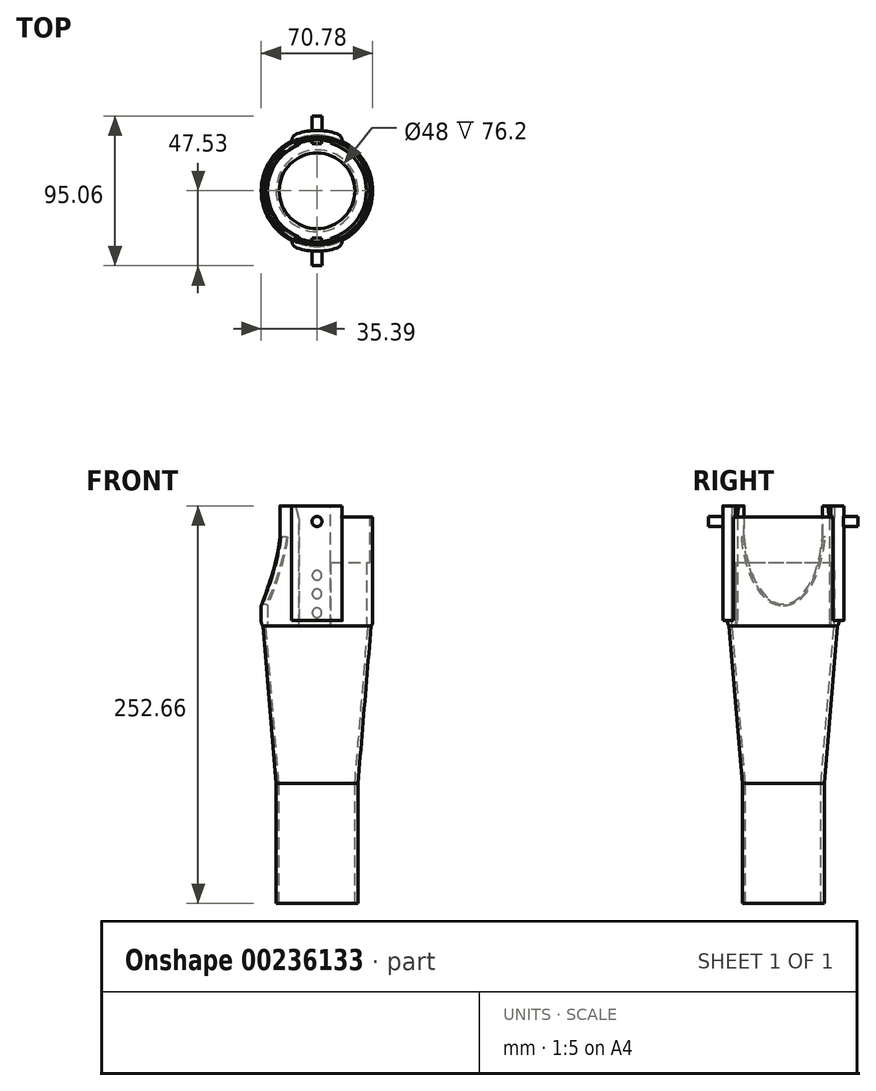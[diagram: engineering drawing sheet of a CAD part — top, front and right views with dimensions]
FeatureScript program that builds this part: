
annotation { "Feature Type Name" : "Feature", "Feature Type Description" : "" }
export const myFeature = defineFeature(function(context is Context, id is Id, definition is map)
    precondition{}
    {
        {
            var Q0;
            Q0=qCreatedBy(makeId("Top.planeOp"),FACE);
            var sketch = newSketch(context, id + "F0", { "sketchPlane" : qUnion([Q0])});
            skCircle(sketch, "E0", {"center": v(0, 0) * mm, "radius": 26 * mm});
            skSolve(sketch);
        }
        {
            var Q0;
            Q0=makeQuery(id+"F0.imprint","IMPRINT",FACE,{"disambiguationData":[TD([[makeQuery(id+"F0.imprint","IMPRINT",EDGE,{"derivedFrom":sQuery(id+"F0.wireOp",EDGE,"E0")}),1.0]])]});
            extrude(context, id + "F1", {"entities" : qUnion([Q0]), "depth" : 76.2 * mm});
        }
        {
            var Q0;
            Q0=makeQuery(id+"F1.opExtrude","CAP_FACE",FACE,{"disambiguationData":[OSD([sQuery(id+"F0.wireOp",EDGE,"E0")])],"isStart":false});
            cPlane(context, id + "F2", {"entities" : qUnion([Q0]), "cplaneType" : CPlaneType.OFFSET, "offset" : 0 * mm, "width" : 150 * mm, "height" : 150 * mm});
        }
        {
            var Q0;
            Q0=qCreatedBy(id+"F2.planeOp",FACE);
            var sketch = newSketch(context, id + "F3", { "sketchPlane" : qUnion([Q0])});
            skCircle(sketch, "E1.0", {"center": v(0, 0) * mm, "radius": 26 * mm});
            skSolve(sketch);
        }
        {
            var Q0;
            Q0=qCreatedBy(id+"F2.planeOp",FACE);
            cPlane(context, id + "F4", {"entities" : qUnion([Q0]), "cplaneType" : CPlaneType.OFFSET, "offset" : 100 * mm, "width" : 150 * mm, "height" : 150 * mm});
        }
        {
            var Q0;
            Q0=qCreatedBy(id+"F4.planeOp",FACE);
            var sketch = newSketch(context, id + "F5", { "sketchPlane" : qUnion([Q0])});
            skCircle(sketch, "E2", {"center": v(0, 0) * mm, "radius": 34.38 * mm});
            skSolve(sketch);
        }
        {
            var Q1;
            Q1=makeQuery(id+"F3.imprint","IMPRINT",FACE,{"disambiguationData":[TD([[makeQuery(id+"F3.imprint","IMPRINT",EDGE,{"derivedFrom":sQuery(id+"F3.wireOp",EDGE,"E1.0")}),1.0]])]});
            var Q2;
            Q2=makeQuery(id+"F5.imprint","IMPRINT",FACE,{"disambiguationData":[TD([[makeQuery(id+"F5.imprint","IMPRINT",EDGE,{"derivedFrom":sQuery(id+"F5.wireOp",EDGE,"E2")}),1.0]])]});
            var Q3;
            Q3=sQuery(id+"F5.wireOp",EDGE,"E2");
            var Q4;
            Q4=sQuery(id+"F3.wireOp",EDGE,"E1.0");
            loft(context, id + "F6", {"operationType" : NewBodyOperationType.ADD, "sheetProfilesArray" : [{ "sheetProfileEntities" : qUnion([Q1]) }, { "sheetProfileEntities" : qUnion([Q2]) }], "wireProfilesArray" : [{ "wireProfileEntities" : qUnion([Q3]) }, { "wireProfileEntities" : qUnion([Q4]) }]});
        }
        {
            var Q0;
            Q0=qCreatedBy(id+"F2.planeOp",FACE);
            var sketch = newSketch(context, id + "F7", { "sketchPlane" : qUnion([Q0])});
            skCircle(sketch, "E3", {"center": v(0, 0) * mm, "radius": 24 * mm});
            skSolve(sketch);
        }
        {
            var Q0;
            Q0=qCreatedBy(id+"F4.planeOp",FACE);
            var sketch = newSketch(context, id + "F8", { "sketchPlane" : qUnion([Q0])});
            skCircle(sketch, "E4", {"center": v(0, 0) * mm, "radius": 32.38 * mm});
            skCircle(sketch, "E5.0", {"center": v(0, 0) * mm, "radius": 34.38 * mm, "construction": true});
            skSolve(sketch);
        }
        {
            var Q1;
            Q1=qSketchRegion(id+"F7",true);
            var Q2;
            Q2=qSketchRegion(id+"F8",true);
            loft(context, id + "F9", {"operationType" : NewBodyOperationType.REMOVE, "sheetProfilesArray" : [{ "sheetProfileEntities" : qUnion([Q1]) }, { "sheetProfileEntities" : qUnion([Q2]) }]});
        }
        {
            var Q0;
            Q0=qCreatedBy(makeId("Top.planeOp"),FACE);
            var sketch = newSketch(context, id + "F10", { "sketchPlane" : qUnion([Q0])});
            skCircle(sketch, "E6", {"center": v(0, 0) * mm, "radius": 24 * mm});
            skSolve(sketch);
        }
        {
            var Q1;
            Q1=qSketchRegion(id+"F7",true);
            var Q2;
            Q2=qSketchRegion(id+"F10",true);
            loft(context, id + "F11", {"operationType" : NewBodyOperationType.REMOVE, "sheetProfilesArray" : [{ "sheetProfileEntities" : qUnion([Q1]) }, { "sheetProfileEntities" : qUnion([Q2]) }]});
        }
        {
            var Q0;
            Q0=qCreatedBy(id+"F4.planeOp",FACE);
            var sketch = newSketch(context, id + "F12", { "sketchPlane" : qUnion([Q0])});
            skCircle(sketch, "E7.0", {"center": v(0, 0) * mm, "radius": 32.38 * mm, "construction": true});
            skCircle(sketch, "E8.0", {"center": v(0, 0) * mm, "radius": 34.38 * mm, "construction": true});
            skCircle(sketch, "E9", {"center": v(0, 0) * mm, "radius": 31.38 * mm});
            skCircle(sketch, "E10", {"center": v(0, 0) * mm, "radius": 35.38 * mm});
            skSolve(sketch);
        }
        {
            var Q0;
            Q0=qSketchRegion(id+"F12",true);
            extrude(context, id + "F13", {"entities" : qUnion([Q0]), "operationType" : NewBodyOperationType.ADD, "depth" : 56.46 * mm});
        }
        {
            var Q0;
            Q0=makeQuery(id+"F13.opExtrude","CAP_EDGE",EDGE,{"disambiguationData":[OSD([sQuery(id+"F12.wireOp",EDGE,"E10")])],"isStart":true});
            fillet(context, id + "F14", {"entities" : qUnion([Q0]), "radius" : 5 * mm, "tangentPropagation" : true, "allowEdgeOverflow" : false});
        }
        {
            var Q0;
            Q0=makeQuery(id+"F13.opExtrude","CAP_FACE",FACE,{"disambiguationData":[OSD([sQuery(id+"F12.wireOp",EDGE,"E9"),sQuery(id+"F12.wireOp",EDGE,"E10")])],"isStart":false});
            cPlane(context, id + "F15", {"entities" : qUnion([Q0]), "cplaneType" : CPlaneType.OFFSET, "offset" : 0 * mm, "width" : 150 * mm, "height" : 150 * mm});
        }
        {
            var Q0;
            Q0=qCreatedBy(id+"F15.planeOp",FACE);
            var sketch = newSketch(context, id + "F16", { "sketchPlane" : qUnion([Q0])});
            skArc(sketch, "E11", {"start": v(8.5, -32.53) * mm, "mid": v(33.63, 0) * mm, "end": v(8.5, 32.53) * mm});
            skArc(sketch, "E12", {"start": v(8.5, -27.2) * mm, "mid": v(28.5, 0) * mm, "end": v(8.5, 27.2) * mm});
            skLineSegment(sketch, "E13", {"start": v(0, 46.86) * mm, "end": v(0, -51.58) * mm, "construction": true});
            skLineSegment(sketch, "E14", {"start": v(8.5, 46.54) * mm, "end": v(8.5, -40.4) * mm, "construction": true});
            skLineSegment(sketch, "E15", {"start": v(8.5, 27.2) * mm, "end": v(8.5, 32.53) * mm});
            skLineSegment(sketch, "E16", {"start": v(8.5, -32.53) * mm, "end": v(8.5, -27.2) * mm});
            skSolve(sketch);
        }
        {
            var Q0;
            Q0=qSketchRegion(id+"F16",true);
            extrude(context, id + "F17", {"entities" : qUnion([Q0]), "operationType" : NewBodyOperationType.REMOVE, "oppositeDirection" : true, "depth" : 16 * mm});
        }
        {
            var Q0;
            Q0=qCreatedBy(id+"F15.planeOp",FACE);
            var sketch = newSketch(context, id + "F18", { "sketchPlane" : qUnion([Q0])});
            skPoint(sketch, "E17.0", {"position": v(8.5, 32.53) * mm});
            skPoint(sketch, "E18.0", {"position": v(8.5, -32.53) * mm});
            skLineSegment(sketch, "E19.bottom", {"start": v(8.5, 32.53) * mm, "end": v(-11.5, 32.53) * mm});
            skLineSegment(sketch, "E19.top", {"start": v(8.5, 22.91) * mm, "end": v(-11.5, 22.91) * mm});
            skLineSegment(sketch, "E19.left", {"start": v(8.5, 32.53) * mm, "end": v(8.5, 22.91) * mm});
            skLineSegment(sketch, "E19.right", {"start": v(-11.5, 32.53) * mm, "end": v(-11.5, 22.91) * mm});
            skLineSegment(sketch, "E20.bottom", {"start": v(8.5, -32.53) * mm, "end": v(-11.5, -32.53) * mm});
            skLineSegment(sketch, "E20.top", {"start": v(8.5, -22) * mm, "end": v(-11.5, -22) * mm});
            skLineSegment(sketch, "E20.left", {"start": v(8.5, -32.53) * mm, "end": v(8.5, -22) * mm});
            skLineSegment(sketch, "E20.right", {"start": v(-11.5, -32.53) * mm, "end": v(-11.5, -22) * mm});
            skSolve(sketch);
        }
        {
            var Q0;
            Q0=qSketchRegion(id+"F18",true);
            extrude(context, id + "F19", {"entities" : qUnion([Q0]), "operationType" : NewBodyOperationType.REMOVE, "oppositeDirection" : true, "depth" : 56.46 * mm});
        }
        {
            var Q0;
            {var subQ0=sQuery(id+"F12.wireOp",EDGE,"E9");Q0=makeQuery(id+"F19.boolean.opBoolean","SPLIT",EDGE,{"disambiguationData":[TD([makeQuery(id+"F19.opExtrude","SWEPT_FACE",FACE,{"disambiguationData":[OSD([sQuery(id+"F18.wireOp",EDGE,"E19.right")])]})])],"derivedFrom":makeQuery(id+"F13.opExtrude","CAP_EDGE",EDGE,{"disambiguationData":[OSD([subQ0])],"isStart":true})});}
            var Q1;
            {var subQ0=sQuery(id+"F12.wireOp",EDGE,"E9");Q1=makeQuery(id+"F19.boolean.opBoolean","SPLIT",EDGE,{"disambiguationData":[TD([makeQuery(id+"F19.opExtrude","SWEPT_FACE",FACE,{"disambiguationData":[OSD([sQuery(id+"F18.wireOp",EDGE,"E19.left")])]})])],"derivedFrom":makeQuery(id+"F13.opExtrude","CAP_EDGE",EDGE,{"disambiguationData":[OSD([subQ0])],"isStart":true})});}
            fillet(context, id + "F20", {"entities" : qUnion([Q0, Q1]), "radius" : 5 * mm, "tangentPropagation" : true, "allowEdgeOverflow" : false});
        }
        {
            var Q0;
            Q0=makeQuery(id+"F19.boolean.opBoolean","COPY",FACE,{"derivedFrom":makeQuery(id+"F19.opExtrude","SWEPT_FACE",FACE,{"disambiguationData":[OSD([sQuery(id+"F18.wireOp",EDGE,"E19.bottom")])]})});
            cPlane(context, id + "F21", {"entities" : qUnion([Q0]), "cplaneType" : CPlaneType.OFFSET, "offset" : 0 * mm, "width" : 150 * mm, "height" : 150 * mm});
        }
        {
            var Q0;
            Q0=qCreatedBy(id+"F21.planeOp",FACE);
            var sketch = newSketch(context, id + "F22", { "sketchPlane" : qUnion([Q0])});
            skLineSegment(sketch, "E21.0.0", {"start": v(8.5, 232.66) * mm, "end": v(-11.5, 232.66) * mm, "construction": true});
            skLineSegment(sketch, "E21.0.1", {"start": v(-11.5, 232.66) * mm, "end": v(-11.5, 176.2) * mm, "construction": true});
            skLineSegment(sketch, "E21.0.2", {"start": v(-11.5, 176.2) * mm, "end": v(8.5, 176.2) * mm, "construction": true});
            skLineSegment(sketch, "E21.0.3", {"start": v(8.5, 176.2) * mm, "end": v(8.5, 216.66) * mm, "construction": true});
            skLineSegment(sketch, "E21.0.4", {"start": v(8.5, 216.66) * mm, "end": v(8.5, 232.66) * mm, "construction": true});
            skLineSegment(sketch, "E22", {"start": v(0, 232.66) * mm, "end": v(0, 176.2) * mm, "construction": true});
            skCircle(sketch, "E23", {"center": v(0, 184.7) * mm, "radius": 3 * mm});
            skCircle(sketch, "E24", {"center": v(0, 196.7) * mm, "radius": 3 * mm});
            skCircle(sketch, "E25", {"center": v(0, 208.45) * mm, "radius": 3 * mm});
            skSolve(sketch);
        }
        {
            var Q0;
            Q0=qSketchRegion(id+"F22",true);
            extrude(context, id + "F23", {"entities" : qUnion([Q0]), "depth" : 2.5 * mm});
        }
        {
            var Q0;
            Q0=makeQuery(id+"F23.opExtrude","SWEPT_BODY",BODY,{"disambiguationData":[OSD([sQuery(id+"F22.wireOp",EDGE,"E25")])]});
            var Q1;
            Q1=makeQuery(id+"F23.opExtrude","SWEPT_BODY",BODY,{"disambiguationData":[OSD([sQuery(id+"F22.wireOp",EDGE,"E24")])]});
            var Q2;
            Q2=makeQuery(id+"F23.opExtrude","SWEPT_BODY",BODY,{"disambiguationData":[OSD([sQuery(id+"F22.wireOp",EDGE,"E23")])]});
            var Q3;
            Q3=qCreatedBy(makeId("Front.planeOp"),FACE);
            mirror(context, id + "F24", {"operationType" : NewBodyOperationType.ADD, "entities" : qUnion([Q0, Q1, Q2]), "mirrorPlane" : qUnion([Q3])});
        }
        {
            var Q0;
            Q0=qCreatedBy(id+"F15.planeOp",FACE);
            var sketch = newSketch(context, id + "F25", { "sketchPlane" : qUnion([Q0])});
            skArc(sketch, "E26.0", {"start": v(16, 31.56) * mm, "mid": v(0, 35.38) * mm, "end": v(-16, 31.56) * mm});
            skArc(sketch, "E27.0", {"start": v(16, 34.9) * mm, "mid": v(0, 38.39) * mm, "end": v(-16, 34.9) * mm});
            skLineSegment(sketch, "E28", {"start": v(0, 53.23) * mm, "end": v(0, -112.73) * mm, "construction": true});
            skLineSegment(sketch, "E29", {"start": v(16, 34.9) * mm, "end": v(16, 31.56) * mm});
            skLineSegment(sketch, "E30.MirrorCS", {"start": v(-16, 34.9) * mm, "end": v(-16, 31.56) * mm});
            skLineSegment(sketch, "E31.trimOffspring", {"start": v(-16, -31.56) * mm, "end": v(-16, -34.9) * mm});
            skLineSegment(sketch, "E32.trimOffspring", {"start": v(16, -31.56) * mm, "end": v(16, -34.9) * mm});
            skArc(sketch, "E33.trimOffspring", {"start": v(-16, -34.9) * mm, "mid": v(0, -38.39) * mm, "end": v(16, -34.9) * mm});
            skArc(sketch, "E34.trimOffspring", {"start": v(-16, -31.56) * mm, "mid": v(0, -35.38) * mm, "end": v(16, -31.56) * mm});
            skSolve(sketch);
        }
        {
            var Q0;
            Q0=makeQuery(id+"F25.imprint","IMPRINT",FACE,{"disambiguationData":[TD([[makeQuery(id+"F25.imprint","IMPRINT",EDGE,{"derivedFrom":sQuery(id+"F25.wireOp",EDGE,"E26.0")}),-1.0]])]});
            var Q1;
            Q1=makeQuery(id+"F25.imprint","IMPRINT",FACE,{"disambiguationData":[TD([[makeQuery(id+"F25.imprint","IMPRINT",EDGE,{"derivedFrom":sQuery(id+"F25.wireOp",EDGE,"E31.trimOffspring")}),1.0]])]});
            extrude(context, id + "F26", {"entities" : qUnion([Q0, Q1]), "operationType" : NewBodyOperationType.ADD, "depth" : 20 * mm, "hasSecondDirection" : true, "secondDirectionOppositeDirection" : true, "secondDirectionDepth" : 53 * mm});
        }
        {
            var Q0;
            Q0=makeQuery(id+"F13.opExtrude","CAP_FACE",FACE,{"disambiguationData":[OSD([sQuery(id+"F12.wireOp",EDGE,"E9"),sQuery(id+"F12.wireOp",EDGE,"E10")])],"isStart":false});
            var sketch = newSketch(context, id + "F27", { "sketchPlane" : qUnion([Q0])});
            skArc(sketch, "E35.0", {"start": v(-11.5, 29.2) * mm, "mid": v(-13.8, 28.2) * mm, "end": v(-16, 27) * mm});
            skArc(sketch, "E36.0", {"start": v(16, 31.56) * mm, "mid": v(0, 35.39) * mm, "end": v(-16, 31.56) * mm});
            skLineSegment(sketch, "E36.1", {"start": v(8.5, 32.53) * mm, "end": v(-11.5, 32.53) * mm});
            skArc(sketch, "E36.2", {"start": v(8.5, -32.53) * mm, "mid": v(12.34, -31.28) * mm, "end": v(16, -29.57) * mm});
            skLineSegment(sketch, "E36.3", {"start": v(-11.5, 32.53) * mm, "end": v(-11.5, 29.2) * mm});
            skArc(sketch, "E37.0", {"start": v(-16, -31.56) * mm, "mid": v(0, -35.38) * mm, "end": v(16, -31.56) * mm});
            skLineSegment(sketch, "E38.0", {"start": v(8.5, -32.53) * mm, "end": v(-11.5, -32.53) * mm});
            skLineSegment(sketch, "E39.0", {"start": v(-11.5, -32.53) * mm, "end": v(-11.5, -29.2) * mm});
            skLineSegment(sketch, "E40", {"start": v(-16, -31.56) * mm, "end": v(-16, -27) * mm});
            skLineSegment(sketch, "E41", {"start": v(16, -31.56) * mm, "end": v(16, -29.57) * mm});
            skLineSegment(sketch, "E42", {"start": v(-16, 31.56) * mm, "end": v(-16, 27) * mm});
            skLineSegment(sketch, "E43", {"start": v(16, 31.56) * mm, "end": v(16, 29.57) * mm});
            skArc(sketch, "E44.trimOffspring", {"start": v(-16, -27) * mm, "mid": v(-13.8, -28.2) * mm, "end": v(-11.5, -29.2) * mm});
            skArc(sketch, "E45.trimOffspring", {"start": v(16, 29.57) * mm, "mid": v(12.34, 31.28) * mm, "end": v(8.5, 32.53) * mm});
            skSolve(sketch);
        }
        {
            var Q0;
            Q0=makeQuery(id+"F27.imprint","IMPRINT",FACE,{"disambiguationData":[TD([[makeQuery(id+"F27.imprint","IMPRINT",EDGE,{"derivedFrom":sQuery(id+"F27.wireOp",EDGE,"E36.2")}),-1.0]])]});
            var Q1;
            Q1=makeQuery(id+"F27.imprint","IMPRINT",FACE,{"disambiguationData":[TD([[makeQuery(id+"F27.imprint","IMPRINT",EDGE,{"derivedFrom":sQuery(id+"F27.wireOp",EDGE,"E35.0")}),-1.0]])]});
            extrude(context, id + "F28", {"entities" : qUnion([Q0, Q1]), "operationType" : NewBodyOperationType.ADD, "depth" : 20 * mm, "hasSecondDirection" : true, "secondDirectionOppositeDirection" : true, "secondDirectionDepth" : 25 * mm});
        }
        {
            var Q0;
            Q0=makeQuery(id+"F26.opExtrude","SWEPT_EDGE",EDGE,{"disambiguationData":[OSD([sQuery(id+"F25.wireOp",EDGE,"E32.trimOffspring"),sQuery(id+"F25.wireOp",EDGE,"E33.trimOffspring")])]});
            var Q1;
            Q1=makeQuery(id+"F26.opExtrude","SWEPT_EDGE",EDGE,{"disambiguationData":[OSD([sQuery(id+"F25.wireOp",EDGE,"E31.trimOffspring"),sQuery(id+"F25.wireOp",EDGE,"E33.trimOffspring")])]});
            var Q2;
            Q2=makeQuery(id+"F26.opExtrude","SWEPT_EDGE",EDGE,{"disambiguationData":[OSD([sQuery(id+"F25.wireOp",EDGE,"E27.0"),sQuery(id+"F25.wireOp",EDGE,"E29")])]});
            var Q3;
            Q3=makeQuery(id+"F26.opExtrude","SWEPT_EDGE",EDGE,{"disambiguationData":[OSD([sQuery(id+"F25.wireOp",EDGE,"E27.0"),sQuery(id+"F25.wireOp",EDGE,"E30.MirrorCS")])]});
            fillet(context, id + "F29", {"entities" : qUnion([Q0, Q1, Q2, Q3]), "radius" : 5 * mm, "tangentPropagation" : true, "allowEdgeOverflow" : false});
        }
        {
            var Q0;
            Q0=makeQuery(id+"F28.opExtrude","SWEPT_EDGE",EDGE,{"disambiguationData":[OSD([sQuery(id+"F12.wireOp",EDGE,"E9"),sQuery(id+"F27.wireOp",EDGE,"E40"),sQuery(id+"F27.wireOp",EDGE,"E44.trimOffspring")])]});
            fillet(context, id + "F30", {"entities" : qUnion([Q0]), "radius" : 1 * mm, "tangentPropagation" : true, "allowEdgeOverflow" : false});
        }
        {
            var Q0;
            Q0=makeQuery(id+"F28.opExtrude","SWEPT_EDGE",EDGE,{"disambiguationData":[OSD([sQuery(id+"F16.wireOp",EDGE,"E11"),sQuery(id+"F27.wireOp",EDGE,"E36.2"),sQuery(id+"F27.wireOp",EDGE,"E41")])]});
            fillet(context, id + "F31", {"entities" : qUnion([Q0]), "radius" : 1 * mm, "tangentPropagation" : true, "allowEdgeOverflow" : false});
        }
        {
            var Q0;
            Q0=makeQuery(id+"F28.opExtrude","SWEPT_EDGE",EDGE,{"disambiguationData":[OSD([sQuery(id+"F16.wireOp",EDGE,"492040e4-c0d6-4e85-9304-9fc9be24122b"),sQuery(id+"F27.wireOp",EDGE,"7227a9f5-6aaa-42c1-b2d3-e79f72207cf60.MirrorCS")])]});
            var Q1;
            Q1=makeQuery(id+"F28.opExtrude","SWEPT_EDGE",EDGE,{"disambiguationData":[OSD([sQuery(id+"F12.wireOp",EDGE,"E9"),sQuery(id+"F27.wireOp",EDGE,"E35.0"),sQuery(id+"F27.wireOp",EDGE,"E42")])]});
            fillet(context, id + "F32", {"entities" : qUnion([Q0, Q1]), "radius" : 1 * mm, "tangentPropagation" : true, "allowEdgeOverflow" : false});
        }
        {
            var Q0;
            Q0=makeQuery(id+"F28.opExtrude","SWEPT_EDGE",EDGE,{"disambiguationData":[OSD([sQuery(id+"F16.wireOp",EDGE,"E11"),sQuery(id+"F27.wireOp",EDGE,"E43"),sQuery(id+"F27.wireOp",EDGE,"E45.trimOffspring")])]});
            fillet(context, id + "F33", {"entities" : qUnion([Q0]), "radius" : 1 * mm, "tangentPropagation" : true, "allowEdgeOverflow" : false});
        }
        {
            var Q0;
            Q0=makeQuery(id+"F28.boolean.opBoolean","MERGE",FACE,{"derivedFrom":[makeQuery(id+"F19.boolean.opBoolean","COPY",FACE,{"derivedFrom":makeQuery(id+"F19.opExtrude","SWEPT_FACE",FACE,{"disambiguationData":[OSD([sQuery(id+"F18.wireOp",EDGE,"E19.bottom")])]})}),makeQuery(id+"F28.opExtrude","SWEPT_FACE",FACE,{"disambiguationData":[OSD([sQuery(id+"F27.wireOp",EDGE,"E36.1")])]})]});
            var sketch = newSketch(context, id + "F34", { "sketchPlane" : qUnion([Q0])});
            skLineSegment(sketch, "E46", {"start": v(0, 258) * mm, "end": v(0, 211.42) * mm, "construction": true});
            skCircle(sketch, "E47", {"center": v(0, 242.66) * mm, "radius": 3.18 * mm});
            skSolve(sketch);
        }
        {
            var Q0;
            Q0=makeQuery(id+"F34.imprint","IMPRINT",FACE,{"disambiguationData":[TD([[makeQuery(id+"F34.imprint","IMPRINT",EDGE,{"derivedFrom":sQuery(id+"F34.wireOp",EDGE,"E47")}),1.0]])]});
            extrude(context, id + "F35", {"entities" : qUnion([Q0]), "oppositeDirection" : true, "depth" : 15 * mm});
        }
        {
            var Q0;
            Q0=makeQuery(id+"F35.opExtrude","SWEPT_BODY",BODY,{"disambiguationData":[OSD([sQuery(id+"F34.wireOp",EDGE,"E47")])]});
            var Q1;
            Q1=qCreatedBy(makeId("Front.planeOp"),FACE);
            mirror(context, id + "F36", {"operationType" : NewBodyOperationType.ADD, "entities" : qUnion([Q0]), "mirrorPlane" : qUnion([Q1])});
        }
        {
            var Q0;
            Q0=qCreatedBy(makeId("Right.planeOp"),FACE);
            cPlane(context, id + "F37", {"entities" : qUnion([Q0]), "cplaneType" : CPlaneType.OFFSET, "offset" : 55 * mm, "oppositeDirection" : true, "width" : 150 * mm, "height" : 150 * mm});
        }
        {
            var Q0;
            Q0=qCreatedBy(id+"F37.planeOp",FACE);
            var sketch = newSketch(context, id + "F38", { "sketchPlane" : qUnion([Q0])});
            skEllipse(sketch, "E48", {"center": v(0, 241.57) * mm, "majorRadius": 25.3 * mm, "minorRadius": 51.5 * mm, "majorAxis": v(-1, 0)});
            skSolve(sketch);
        }
        {
            var Q0;
            Q0=qSketchRegion(id+"F38",true);
            extrude(context, id + "F39", {"entities" : qUnion([Q0]), "operationType" : NewBodyOperationType.REMOVE, "depth" : 40 * mm});
        }
        {
            var Q0;
            Q0=makeQuery(id+"F39.boolean.opBoolean","INTERSECT",EDGE,{"derivedFrom":[makeQuery(id+"F13.opExtrude","SWEPT_FACE",FACE,{"disambiguationData":[OSD([sQuery(id+"F12.wireOp",EDGE,"E10")])]}),makeQuery(id+"F39.opExtrude","SWEPT_FACE",FACE,{"disambiguationData":[OSD([sQuery(id+"F38.wireOp",EDGE,"E48")])]})]});
            var Q1;
            {var subQ1=sQuery(id+"F12.wireOp",EDGE,"E9");Q1=makeQuery(id+"F39.boolean.opBoolean","INTERSECT",EDGE,{"derivedFrom":[makeQuery(id+"F28.boolean.opBoolean","MERGE",FACE,{"derivedFrom":[makeQuery(id+"F19.boolean.opBoolean","SPLIT",FACE,{"disambiguationData":[TD([makeQuery(id+"F19.opExtrude","SWEPT_FACE",FACE,{"disambiguationData":[OSD([sQuery(id+"F18.wireOp",EDGE,"E19.right")])]})])],"derivedFrom":makeQuery(id+"F13.opExtrude","SWEPT_FACE",FACE,{"disambiguationData":[OSD([subQ1])]})}),makeQuery(id+"F28.opExtrude","SWEPT_FACE",FACE,{"disambiguationData":[OSD([sQuery(id+"F27.wireOp",EDGE,"E35.0")])]}),makeQuery(id+"F28.opExtrude","SWEPT_FACE",FACE,{"disambiguationData":[OSD([sQuery(id+"F27.wireOp",EDGE,"E44.trimOffspring")])]})]}),makeQuery(id+"F39.opExtrude","SWEPT_FACE",FACE,{"disambiguationData":[OSD([sQuery(id+"F38.wireOp",EDGE,"E48")])]})]});}
            fillet(context, id + "F40", {"entities" : qUnion([Q0, Q1]), "radius" : 1 * mm, "tangentPropagation" : true, "allowEdgeOverflow" : false});
        }
        {
            var Q0;
            {var subQ1=sQuery(id+"F25.wireOp",EDGE,"E31.trimOffspring");var subQ2=makeQuery(id+"F26.opExtrude","SWEPT_FACE",FACE,{"disambiguationData":[OSD([subQ1])]});var subQ3=sQuery(id+"F12.wireOp",EDGE,"E10");var subQ7=sQuery(id+"F12.wireOp",EDGE,"E9");var subQ8=makeQuery(id+"F13.opExtrude","SWEPT_FACE",FACE,{"disambiguationData":[OSD([subQ7])]});Q0=makeQuery(id+"F39.boolean.opBoolean","SPLIT",FACE,{"disambiguationData":[TD([subQ2])],"derivedFrom":makeQuery(id+"F28.boolean.opBoolean","SPLIT",FACE,{"disambiguationData":[TD([subQ8])],"derivedFrom":makeQuery(id+"F13.opExtrude","CAP_FACE",FACE,{"disambiguationData":[OSD([subQ7,subQ3])],"isStart":false})})});}
            var Q1;
            {var subQ2=sQuery(id+"F25.wireOp",EDGE,"E30.MirrorCS");var subQ3=makeQuery(id+"F26.opExtrude","SWEPT_FACE",FACE,{"disambiguationData":[OSD([subQ2])]});var subQ4=sQuery(id+"F12.wireOp",EDGE,"E10");var subQ7=sQuery(id+"F12.wireOp",EDGE,"E9");var subQ8=makeQuery(id+"F13.opExtrude","SWEPT_FACE",FACE,{"disambiguationData":[OSD([subQ7])]});Q1=makeQuery(id+"F39.boolean.opBoolean","SPLIT",FACE,{"disambiguationData":[TD([subQ3])],"derivedFrom":makeQuery(id+"F28.boolean.opBoolean","SPLIT",FACE,{"disambiguationData":[TD([subQ8])],"derivedFrom":makeQuery(id+"F13.opExtrude","CAP_FACE",FACE,{"disambiguationData":[OSD([subQ7,subQ4])],"isStart":false})})});}
            var Q2;
            Q2=makeQuery(id+"F28.boolean.opBoolean","MERGE",FACE,{"derivedFrom":[makeQuery(id+"F26.opExtrude","CAP_FACE",FACE,{"disambiguationData":[OSD([sQuery(id+"F25.wireOp",EDGE,"E31.trimOffspring"),sQuery(id+"F25.wireOp",EDGE,"E32.trimOffspring"),sQuery(id+"F25.wireOp",EDGE,"E33.trimOffspring"),sQuery(id+"F25.wireOp",EDGE,"E34.trimOffspring")])],"isStart":false}),makeQuery(id+"F28.opExtrude","CAP_FACE",FACE,{"disambiguationData":[OSD([sQuery(id+"F27.wireOp",EDGE,"E36.2"),sQuery(id+"F27.wireOp",EDGE,"E37.0"),sQuery(id+"F27.wireOp",EDGE,"E38.0"),sQuery(id+"F27.wireOp",EDGE,"E39.0"),sQuery(id+"F27.wireOp",EDGE,"E40"),sQuery(id+"F27.wireOp",EDGE,"E41"),sQuery(id+"F27.wireOp",EDGE,"E44.trimOffspring")])],"isStart":false})]});
            extrude(context, id + "F41", {"entities" : qUnion([Q0, Q1]), "operationType" : NewBodyOperationType.ADD, "endBound" : BoundingType.UP_TO_SURFACE, "endBoundEntityFace" : qUnion([Q2]), "depth" : 25 * mm});
        }
        {
            var Q0;
            {var subQ0=sQuery(id+"F12.wireOp",EDGE,"E10");Q0=makeQuery(id+"F28.boolean.opBoolean","SPLIT",FACE,{"disambiguationData":[TD([makeQuery(id+"F17.boolean.opBoolean","COPY",FACE,{"derivedFrom":makeQuery(id+"F17.opExtrude","SWEPT_FACE",FACE,{"disambiguationData":[OSD([sQuery(id+"F16.wireOp",EDGE,"E11")])]})})])],"derivedFrom":makeQuery(id+"F13.opExtrude","CAP_FACE",FACE,{"disambiguationData":[OSD([sQuery(id+"F12.wireOp",EDGE,"E9"),subQ0])],"isStart":false})});}
            extrude(context, id + "F42", {"entities" : qUnion([Q0]), "operationType" : NewBodyOperationType.ADD, "depth" : 13 * mm});
        }
        {
            var Q0;
            Q0=makeQuery(id+"F28.boolean.opBoolean","MERGE",FACE,{"derivedFrom":[makeQuery(id+"F19.boolean.opBoolean","COPY",FACE,{"derivedFrom":makeQuery(id+"F19.opExtrude","SWEPT_FACE",FACE,{"disambiguationData":[OSD([sQuery(id+"F18.wireOp",EDGE,"E19.bottom")])]})}),makeQuery(id+"F28.opExtrude","SWEPT_FACE",FACE,{"disambiguationData":[OSD([sQuery(id+"F27.wireOp",EDGE,"E36.1")])]})]});
            var sketch = newSketch(context, id + "F43", { "sketchPlane" : qUnion([Q0])});
            skLineSegment(sketch, "E49.0", {"start": v(-11.5, 244.66) * mm, "end": v(-11.5, 252.66) * mm});
            skLineSegment(sketch, "E50", {"start": v(-11.5, 252.66) * mm, "end": v(-13.5, 252.66) * mm});
            skLineSegment(sketch, "E51", {"start": v(-13.5, 252.66) * mm, "end": v(-11.5, 244.66) * mm});
            skPoint(sketch, "E52.orphan", {"position": v(-11.5, 176.37) * mm});
            skSolve(sketch);
        }
        {
            var Q0;
            Q0=qSketchRegion(id+"F43",true);
            extrude(context, id + "F44", {"entities" : qUnion([Q0]), "operationType" : NewBodyOperationType.REMOVE, "depth" : 25 * mm});
        }
        {
            var Q0;
            Q0=makeQuery(id+"F28.boolean.opBoolean","MERGE",FACE,{"derivedFrom":[makeQuery(id+"F19.boolean.opBoolean","COPY",FACE,{"derivedFrom":makeQuery(id+"F19.opExtrude","SWEPT_FACE",FACE,{"disambiguationData":[OSD([sQuery(id+"F18.wireOp",EDGE,"E20.bottom")])]})}),makeQuery(id+"F28.opExtrude","SWEPT_FACE",FACE,{"disambiguationData":[OSD([sQuery(id+"F27.wireOp",EDGE,"E38.0")])]})]});
            var sketch = newSketch(context, id + "F45", { "sketchPlane" : qUnion([Q0])});
            skLineSegment(sketch, "E53.0", {"start": v(11.5, 244.66) * mm, "end": v(11.5, 252.66) * mm});
            skLineSegment(sketch, "E54", {"start": v(11.5, 252.66) * mm, "end": v(13.5, 252.66) * mm});
            skLineSegment(sketch, "E55", {"start": v(13.5, 252.66) * mm, "end": v(11.5, 244.66) * mm});
            skPoint(sketch, "E56.orphan", {"position": v(11.5, 176.37) * mm});
            skSolve(sketch);
        }
        {
            var Q0;
            Q0=qSketchRegion(id+"F45",true);
            extrude(context, id + "F46", {"entities" : qUnion([Q0]), "operationType" : NewBodyOperationType.REMOVE, "depth" : 25 * mm});
        }
    });
